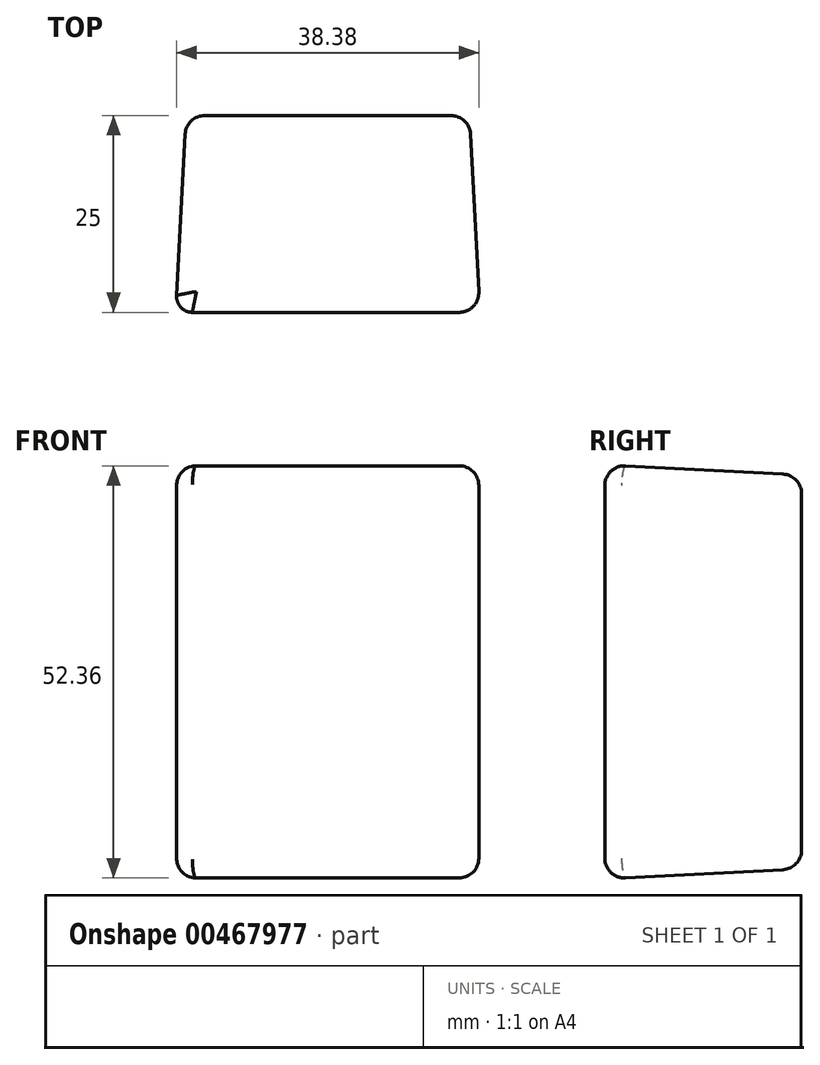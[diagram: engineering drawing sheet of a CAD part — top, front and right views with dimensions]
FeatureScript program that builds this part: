
annotation { "Feature Type Name" : "Feature", "Feature Type Description" : "" }
export const myFeature = defineFeature(function(context is Context, id is Id, definition is map)
    precondition{}
    {
        {
            var Q0;
            Q0=qCreatedBy(makeId("Front.planeOp"),FACE);
            var sketch = newSketch(context, id + "F0", { "sketchPlane" : qUnion([Q0])});
            skLineSegment(sketch, "E0.bottom", {"start": v(12, 25) * mm, "end": v(-24, 25) * mm});
            skLineSegment(sketch, "E0.top", {"start": v(12, -25) * mm, "end": v(-24, -25) * mm});
            skLineSegment(sketch, "E0.left", {"start": v(12, 25) * mm, "end": v(12, -25) * mm});
            skLineSegment(sketch, "E0.right", {"start": v(-24, 25) * mm, "end": v(-24, -25) * mm});
            skSolve(sketch);
        }
        {
            var Q0;
            Q0=makeQuery(id+"F0.imprint","IMPRINT",FACE,{"disambiguationData":[TD([[makeQuery(id+"F0.imprint","IMPRINT",EDGE,{"derivedFrom":sQuery(id+"F0.wireOp",EDGE,"E0.bottom")}),1.0]])]});
            extrude(context, id + "F1", {"entities" : qUnion([Q0]), "depth" : 25 * mm, "hasDraft" : true, "draftAngle" : 3 * degree});
        }
        {
            var Q0;
            Q0=makeQuery(id+"F1.opExtrude","CAP_EDGE",EDGE,{"disambiguationData":[OSD([sQuery(id+"F0.wireOp",EDGE,"E0.right")])],"isStart":false});
            fillet(context, id + "F2", {"entities" : qUnion([Q0]), "radius" : 2 * mm, "allowEdgeOverflow" : false});
        }
        {
            var Q0;
            Q0=makeQuery(id+"F1.opExtrude","SWEPT_EDGE",EDGE,{"disambiguationData":[OSD([sQuery(id+"F0.wireOp",EDGE,"E0.bottom"),sQuery(id+"F0.wireOp",EDGE,"E0.right")])]});
            var Q1;
            Q1=makeQuery(id+"F1.opExtrude","CAP_EDGE",EDGE,{"disambiguationData":[OSD([sQuery(id+"F0.wireOp",EDGE,"E0.right")])],"isStart":true});
            var Q2;
            Q2=makeQuery(id+"F1.opExtrude","SWEPT_EDGE",EDGE,{"disambiguationData":[OSD([sQuery(id+"F0.wireOp",EDGE,"E0.top"),sQuery(id+"F0.wireOp",EDGE,"E0.right")])]});
            var Q3;
            Q3=makeQuery(id+"F1.opExtrude","CAP_EDGE",EDGE,{"disambiguationData":[OSD([sQuery(id+"F0.wireOp",EDGE,"E0.bottom")])],"isStart":false});
            var Q4;
            Q4=makeQuery(id+"F1.opExtrude","CAP_EDGE",EDGE,{"disambiguationData":[OSD([sQuery(id+"F0.wireOp",EDGE,"E0.bottom")])],"isStart":true});
            var Q5;
            Q5=makeQuery(id+"F1.opExtrude","SWEPT_EDGE",EDGE,{"disambiguationData":[OSD([sQuery(id+"F0.wireOp",EDGE,"E0.bottom"),sQuery(id+"F0.wireOp",EDGE,"E0.left")])]});
            var Q6;
            Q6=makeQuery(id+"F1.opExtrude","CAP_EDGE",EDGE,{"disambiguationData":[OSD([sQuery(id+"F0.wireOp",EDGE,"E0.left")])],"isStart":false});
            var Q7;
            Q7=makeQuery(id+"F1.opExtrude","CAP_EDGE",EDGE,{"disambiguationData":[OSD([sQuery(id+"F0.wireOp",EDGE,"E0.top")])],"isStart":false});
            var Q8;
            Q8=makeQuery(id+"F1.opExtrude","SWEPT_EDGE",EDGE,{"disambiguationData":[OSD([sQuery(id+"F0.wireOp",EDGE,"E0.top"),sQuery(id+"F0.wireOp",EDGE,"E0.left")])]});
            var Q9;
            Q9=makeQuery(id+"F1.opExtrude","CAP_EDGE",EDGE,{"disambiguationData":[OSD([sQuery(id+"F0.wireOp",EDGE,"E0.top")])],"isStart":true});
            var Q10;
            Q10=makeQuery(id+"F1.opExtrude","CAP_EDGE",EDGE,{"disambiguationData":[OSD([sQuery(id+"F0.wireOp",EDGE,"E0.left")])],"isStart":true});
            fillet(context, id + "F3", {"entities" : qUnion([Q0, Q1, Q2, Q3, Q4, Q5, Q6, Q7, Q8, Q9, Q10]), "radius" : 2.5 * mm, "tangentPropagation" : true, "allowEdgeOverflow" : false});
        }
    });
